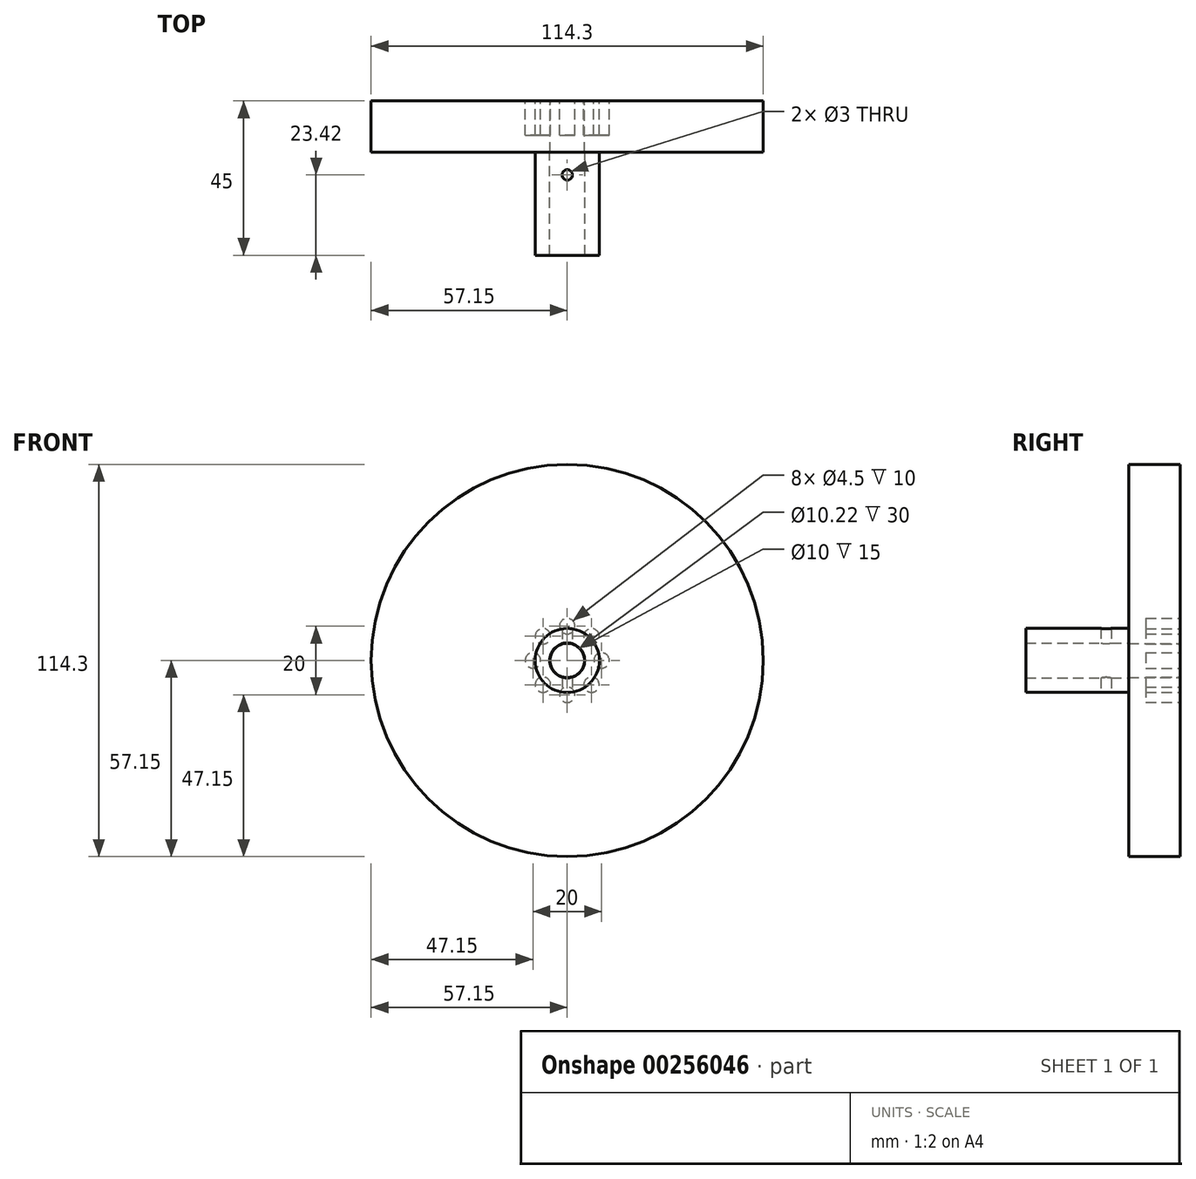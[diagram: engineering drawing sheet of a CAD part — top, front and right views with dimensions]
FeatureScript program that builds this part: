
annotation { "Feature Type Name" : "Feature", "Feature Type Description" : "" }
export const myFeature = defineFeature(function(context is Context, id is Id, definition is map)
    precondition{}
    {
        {
            var Q0;
            Q0=qCreatedBy(makeId("Front.planeOp"),FACE);
            var sketch = newSketch(context, id + "F0", { "sketchPlane" : qUnion([Q0])});
            skCircle(sketch, "E0", {"center": v(0, 0) * mm, "radius": 5 * mm});
            skCircle(sketch, "E1", {"center": v(0, 0) * mm, "radius": 57.15 * mm});
            skSolve(sketch);
        }
        {
            var Q0;
            Q0 = qSketchRegion(id + "F0", true);
            extrude(context, id + "F1", {"entities" : qUnion([Q0]), "depth" : 15 * mm});
        }
        {
            var Q0;
            Q0=makeQuery(id+"F1.opExtrude","CAP_FACE",FACE,{"disambiguationData":[OSD([sQuery(id+"F0.wireOp",EDGE,"E0"),sQuery(id+"F0.wireOp",EDGE,"E1")])],"isStart":false});
            var sketch = newSketch(context, id + "F2", { "sketchPlane" : qUnion([Q0])});
            skCircle(sketch, "E2", {"center": v(0, 0) * mm, "radius": 5.1 * mm});
            skCircle(sketch, "E3", {"center": v(0, 0) * mm, "radius": 9.35 * mm});
            skSolve(sketch);
        }
        {
            var Q0;
            Q0 = qSketchRegion(id + "F2", true);
            extrude(context, id + "F3", {"entities" : qUnion([Q0]), "operationType" : NewBodyOperationType.ADD, "depth" : 30 * mm});
        }
        {
            var Q0;
            Q0=qCreatedBy(makeId("Top.planeOp"),FACE);
            var sketch = newSketch(context, id + "F4", { "sketchPlane" : qUnion([Q0])});
            skCircle(sketch, "E4", {"center": v(0, -21.58) * mm, "radius": 1.5 * mm});
            skSolve(sketch);
        }
        {
            var Q0;
            Q0 = qSketchRegion(id + "F4", true);
            extrude(context, id + "F5", {"entities" : qUnion([Q0]), "operationType" : NewBodyOperationType.REMOVE, "endBound" : BoundingType.SYMMETRIC, "depth" : 25.4 * mm});
        }
        {
            var Q0;
            Q0=makeQuery(id+"F1.opExtrude","CAP_FACE",FACE,{"disambiguationData":[OSD([sQuery(id+"F0.wireOp",EDGE,"E0"),sQuery(id+"F0.wireOp",EDGE,"E1")])],"isStart":true});
            var sketch = newSketch(context, id + "F6", { "sketchPlane" : qUnion([Q0])});
            skCircle(sketch, "E5", {"center": v(0, 10) * mm, "radius": 2.25 * mm});
            skCircle(sketch, "E6", {"center": v(7.07, 7.07) * mm, "radius": 2.25 * mm});
            skCircle(sketch, "E7", {"center": v(10, 0) * mm, "radius": 2.25 * mm});
            skCircle(sketch, "E8", {"center": v(0, -10) * mm, "radius": 2.25 * mm});
            skCircle(sketch, "E9", {"center": v(7.07, -7.07) * mm, "radius": 2.25 * mm});
            skCircle(sketch, "E10", {"center": v(-7.07, -7.07) * mm, "radius": 2.25 * mm});
            skCircle(sketch, "E11", {"center": v(-10, 0) * mm, "radius": 2.25 * mm});
            skCircle(sketch, "E12", {"center": v(-7.07, 7.07) * mm, "radius": 2.25 * mm});
            skSolve(sketch);
        }
        {
            var Q0;
            Q0 = qSketchRegion(id + "F6", true);
            extrude(context, id + "F7", {"entities" : qUnion([Q0]), "operationType" : NewBodyOperationType.REMOVE, "oppositeDirection" : true, "depth" : 10 * mm});
        }
    });
